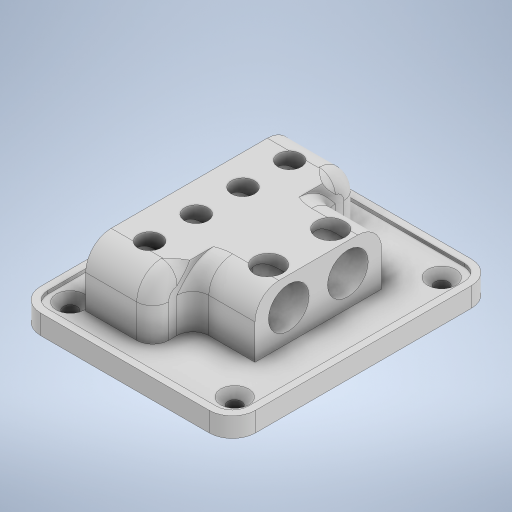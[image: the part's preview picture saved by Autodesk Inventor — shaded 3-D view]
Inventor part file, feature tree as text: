
AUTODESK INVENTOR PART (.ipt)
format: ipt  version: 2023 (Build 270158000, 158)  size: 571,904 bytes
history: native  units: in
note: dims shown in document units (in); Inventor stores cm internally (conversion verified against a paired STEP export)
features: fillet x8, extrude x7, sketch x6, chamfer x1
ambient origin geometry x8: Origin, YZ Plane, XZ Plane, XY Plane, X Axis, Y Axis, Z Axis, Center Point
bodies: Solid1 (feature_tree)
feature tree (22):
  sketch  "Sketch1"  dims[d0=0.1969in d5=0.0886in]
  extrude  "Extrusion1"  Depth=0.1969in
  extrude  "Extrusion2"  Depth=0.2028in TaperAngle=0.0deg
  extrude  "Extrusion3"  Depth=1.5945in
  fillet  "Fillet1"  Radius=0.8268in
  fillet  "Fillet2"  Radius=0.8268in
  fillet  "Fillet3"  Radius=1.2795in
  fillet  "Fillet4"  Radius=1.565in
  fillet  "Fillet5"  Radius=0.7825in
  fillet  "Fillet6"  Radius=0.502in
  fillet  "Fillet7"  Radius=0.7268in
  fillet  "Fillet8"  Radius=0.315in
  extrude  "Extrusion4"  Depth=0.1969in
  extrude  "Extrusion5"  Depth=0.1969in
  extrude  "Extrusion6"  Depth=0.1969in
  extrude  "Extrusion7"  Depth=0.1969in
  chamfer  "Chamfer1"  Distance=0.502in
  sketch  "Sketch2"  dims[d6=0.2028in d7=0.0in d8=0.2421in d9=0.0in]
  sketch  "Sketch3"  dims[d10=2.5591in d11=1.5945in d12=0.8268in d13=0.8268in d14=1.2795in d15=1.565in d16=0.7825in d17=0.502in d18=0.7268in d19=0.0in d20=0.315in]
  sketch  "Sketch4"  dims[d21=0.315in d22=0.1969in]
  sketch  "Sketch5"  dims[d23=0.1969in d24=0.1969in]
  sketch  "Sketch6"  dims[d25=0.1969in d26=0.2953in d27=0.2953in d28=0.502in d29=0.502in d30=0.7303in d31=0.3652in d32=0.3376in d33=0.689in d34=0.0in d35=0.4291in d37=0.5768in d38=0.5768in d39=0.5768in d40=0.3524in d43=0.2884in d44=0.5709in d45=0.0in d46=0.2864in d48=0.3543in d49=0.7677in d51=0.2303in d52=0.3839in d53=0.5768in d54=0.5768in d55=0.5768in d57=0.3755in d58=0.2884in d59=0.2756in d60=0.0in d61=0.1693in d65=0.2362in d66=0.3406in d67=0.3406in d68=0.311in d69=0.3406in d70=0.311in d71=0.3406in d72=0.311in d73=0.2756in d74=0.0in d75=0.0886in d76=0.0492in d77=45.0deg d79=0.311in d80=3.2382in d81=2.6535in d82=1.3268in d83=1.6191in]
